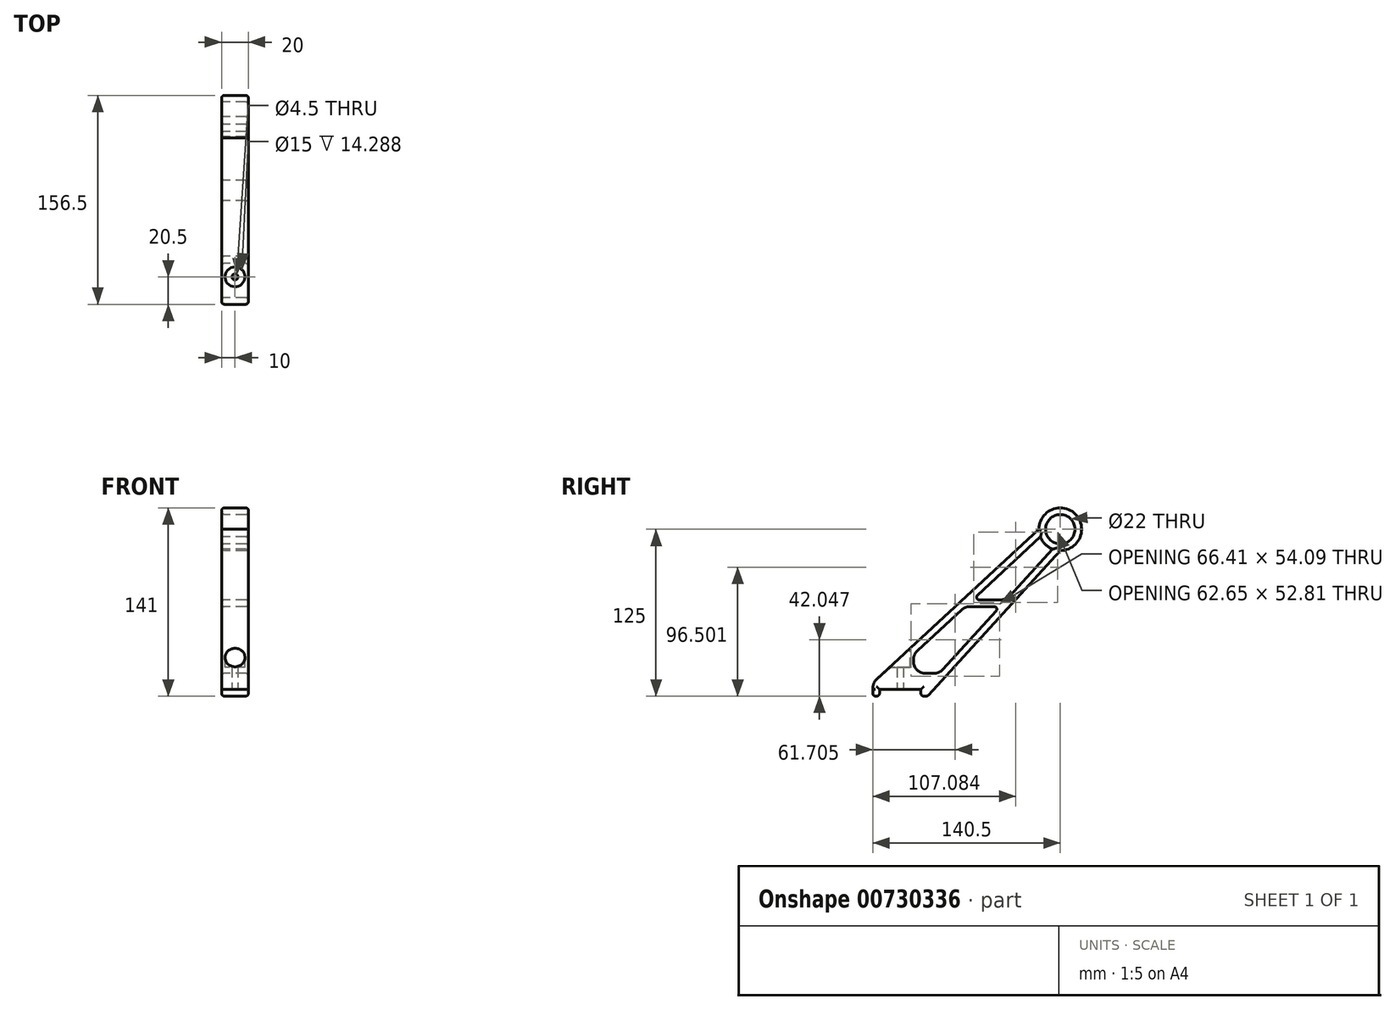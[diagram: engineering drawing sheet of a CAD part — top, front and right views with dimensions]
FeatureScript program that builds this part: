
annotation { "Feature Type Name" : "Feature", "Feature Type Description" : "" }
export const myFeature = defineFeature(function(context is Context, id is Id, definition is map)
    precondition{}
    {
        {
            assignVariable(context, id + "F0", {"name" : "ArmW", "anyValue" : 20});
        }
        {
            var Q0;
            Q0=qCreatedBy(makeId("Right.planeOp"),FACE);
            var sketch = newSketch(context, id + "F1", { "sketchPlane" : qUnion([Q0])});
            skLineSegment(sketch, "E0.bottom", {"start": v(-15.5, 0) * mm, "end": v(15.5, 0) * mm});
            skLineSegment(sketch, "E1.left", {"start": v(-20.47, 1.18) * mm, "end": v(-20.5, 0) * mm});
            skLineSegment(sketch, "E2.left", {"start": v(-20.5, 0) * mm, "end": v(-20.5, -5) * mm});
            skLineSegment(sketch, "E2.right", {"start": v(-15.5, 0) * mm, "end": v(-15.5, -5) * mm});
            skCircle(sketch, "E3", {"center": v(120, 120) * mm, "radius": 11 * mm});
            skCircle(sketch, "E4", {"center": v(120, 120) * mm, "radius": 16 * mm});
            skLineSegment(sketch, "E5.bottom", {"start": v(0, 0) * mm, "end": v(120, 0) * mm, "construction": true});
            skLineSegment(sketch, "E5.top", {"start": v(0, 120) * mm, "end": v(120, 120) * mm, "construction": true});
            skLineSegment(sketch, "E5.left", {"start": v(0, 4.75) * mm, "end": v(0, 120) * mm, "construction": true});
            skLineSegment(sketch, "E5.right", {"start": v(120, 0) * mm, "end": v(120, 120) * mm, "construction": true});
            skLineSegment(sketch, "E6", {"start": v(104, 120) * mm, "end": v(-17.59, 7.6) * mm});
            skLineSegment(sketch, "E7", {"start": v(120, 104) * mm, "end": v(20.5, -5) * mm});
            skLineSegment(sketch, "E8", {"start": v(15.5, 0) * mm, "end": v(15.5, -5) * mm});
            skLineSegment(sketch, "E9", {"start": v(15.5, -5) * mm, "end": v(20.5, -5) * mm});
            skLineSegment(sketch, "E10", {"start": v(-20.5, -5) * mm, "end": v(-15.5, -5) * mm});
            skPoint(sketch, "E11", {"position": v(0, 0) * mm});
            skLineSegment(sketch, "E12", {"start": v(12.9, 28.96) * mm, "end": v(46.14, 59.7) * mm});
            skLineSegment(sketch, "E13", {"start": v(31.93, 14.93) * mm, "end": v(71.92, 58.75) * mm});
            skLineSegment(sketch, "E14", {"start": v(25.28, 12) * mm, "end": v(19, 12) * mm});
            skLineSegment(sketch, "E15", {"start": v(10, 21) * mm, "end": v(10, 22.35) * mm});
            skLineSegment(sketch, "E16", {"start": v(52.25, 62.1) * mm, "end": v(70.44, 62.1) * mm});
            skPoint(sketch, "E17", {"position": v(61.85, 62.1) * mm});
            skLineSegment(sketch, "E18", {"start": v(59.25, 67.1) * mm, "end": v(75.57, 67.1) * mm});
            skPoint(sketch, "E19", {"position": v(66.84, 67.1) * mm});
            skLineSegment(sketch, "E20", {"start": v(10, 26.29) * mm, "end": v(10, 12) * mm});
            skPoint(sketch, "E21.visualSharp", {"position": v(29.25, 12) * mm});
            skArc(sketch, "E21.filletArc", {"start": v(25.28, 12) * mm, "mid": v(28.91, 12.77) * mm, "end": v(31.93, 14.93) * mm});
            skLineSegment(sketch, "E22.trimOffspring", {"start": v(57.9, 70.56) * mm, "end": v(105.09, 114.2) * mm});
            skLineSegment(sketch, "E23.trimOffspring", {"start": v(82.22, 70.03) * mm, "end": v(114.22, 105.08) * mm});
            skPoint(sketch, "E24.visualSharp", {"position": v(48.73, 62.1) * mm});
            skArc(sketch, "E24.filletArc", {"start": v(52.25, 62.1) * mm, "mid": v(48.97, 61.47) * mm, "end": v(46.14, 59.7) * mm});
            skPoint(sketch, "E25.visualSharp", {"position": v(79.54, 67.1) * mm});
            skPoint(sketch, "E26", {"position": v(120, 104) * mm});
            skPoint(sketch, "E27", {"position": v(104, 120) * mm});
            skPoint(sketch, "E28.visualSharp", {"position": v(10, 26.29) * mm});
            skArc(sketch, "E28.filletArc", {"start": v(12.9, 28.96) * mm, "mid": v(10.75, 25.96) * mm, "end": v(10, 22.35) * mm});
            skPoint(sketch, "E29.visualSharp", {"position": v(10, 12) * mm});
            skArc(sketch, "E29.filletArc", {"start": v(10, 21) * mm, "mid": v(12.64, 14.64) * mm, "end": v(19, 12) * mm});
            skPoint(sketch, "E30.visualSharp", {"position": v(74.98, 62.1) * mm});
            skArc(sketch, "E30.filletArc", {"start": v(71.92, 58.75) * mm, "mid": v(72.27, 60.9) * mm, "end": v(70.44, 62.1) * mm});
            skPoint(sketch, "E31.visualSharp", {"position": v(54.14, 67.1) * mm});
            skArc(sketch, "E31.filletArc", {"start": v(57.9, 70.56) * mm, "mid": v(57.39, 68.37) * mm, "end": v(59.25, 67.1) * mm});
            skArc(sketch, "E32.filletArc", {"start": v(75.57, 67.1) * mm, "mid": v(79.2, 67.86) * mm, "end": v(82.22, 70.03) * mm});
            skPoint(sketch, "E33.visualSharp", {"position": v(-20.4, 5) * mm});
            skArc(sketch, "E33.filletArc", {"start": v(-17.59, 7.6) * mm, "mid": v(-19.68, 4.68) * mm, "end": v(-20.47, 1.18) * mm});
            skSolve(sketch);
        }
        {
            var Q0;
            Q0 = qSketchRegion(id + "F1", true);
            extrude(context, id + "F2", {"entities" : qUnion([Q0]), "depth" : (getVariable(context, 'ArmW')) * mm, "offsetDistance" : 25 * mm});
        }
        {
            var Q0;
            Q0=makeQuery(id+"F2.opExtrude","CAP_FACE",FACE,{"disambiguationData":[OSD([sQuery(id+"F1.wireOp",EDGE,"E0.top"),sQuery(id+"F1.wireOp",EDGE,"E0.left"),sQuery(id+"F1.wireOp",EDGE,"E0.right"),sQuery(id+"F1.wireOp",EDGE,"E1.top"),sQuery(id+"F1.wireOp",EDGE,"E1.left"),sQuery(id+"F1.wireOp",EDGE,"NOMvLF7p-otiR-nEAe-fTJC-VMt4UzeXd9s4.top"),sQuery(id+"F1.wireOp",EDGE,"NOMvLF7p-otiR-nEAe-fTJC-VMt4UzeXd9s4.left"),sQuery(id+"F1.wireOp",EDGE,"NOMvLF7p-otiR-nEAe-fTJC-VMt4UzeXd9s4.right"),sQuery(id+"F1.wireOp",EDGE,"E2.top"),sQuery(id+"F1.wireOp",EDGE,"E2.left"),sQuery(id+"F1.wireOp",EDGE,"E2.right"),sQuery(id+"F1.wireOp",EDGE,"ANYR2TeM-pG0v-Sy7E-um98-puJoWqYqz7nG"),sQuery(id+"F1.wireOp",EDGE,"DYsMuk2t-F1yg-EkOE-B9ZC-1FALk9YSir4c"),sQuery(id+"F1.wireOp",EDGE,"ll421e7q-dBxD-7jqP-6ZOg-A462ZdehQbo3"),sQuery(id+"F1.wireOp",EDGE,"fbd24d79-8a35-4fab-bdf5-51f30801ec70.trimOffspring"),sQuery(id+"F1.wireOp",EDGE,"4f573531-568b-457d-87cc-3bfda0ad51ab1.MirrorCS"),sQuery(id+"F1.wireOp",EDGE,"79f8788a-c3f9-4ef8-aa7a-382f7be76f09.trimOffspring"),sQuery(id+"F1.wireOp",EDGE,"E3"),sQuery(id+"F1.wireOp",EDGE,"E4"),sQuery(id+"F1.wireOp",EDGE,"E6"),sQuery(id+"F1.wireOp",EDGE,"E7"),sQuery(id+"F1.wireOp",EDGE,"3807ad3b-ab58-43f6-95fe-ed81e5da2370.filletArc"),sQuery(id+"F1.wireOp",EDGE,"4c582521-ed1f-46d5-8f13-cee76205d209.filletArc")])],"isStart":true});
            var Q1;
            Q1=makeQuery(id+"F2.opExtrude","CAP_FACE",FACE,{"disambiguationData":[OSD([sQuery(id+"F1.wireOp",EDGE,"E0.top"),sQuery(id+"F1.wireOp",EDGE,"E0.left"),sQuery(id+"F1.wireOp",EDGE,"E0.right"),sQuery(id+"F1.wireOp",EDGE,"E1.top"),sQuery(id+"F1.wireOp",EDGE,"E1.left"),sQuery(id+"F1.wireOp",EDGE,"NOMvLF7p-otiR-nEAe-fTJC-VMt4UzeXd9s4.top"),sQuery(id+"F1.wireOp",EDGE,"NOMvLF7p-otiR-nEAe-fTJC-VMt4UzeXd9s4.left"),sQuery(id+"F1.wireOp",EDGE,"NOMvLF7p-otiR-nEAe-fTJC-VMt4UzeXd9s4.right"),sQuery(id+"F1.wireOp",EDGE,"E2.top"),sQuery(id+"F1.wireOp",EDGE,"E2.left"),sQuery(id+"F1.wireOp",EDGE,"E2.right"),sQuery(id+"F1.wireOp",EDGE,"ANYR2TeM-pG0v-Sy7E-um98-puJoWqYqz7nG"),sQuery(id+"F1.wireOp",EDGE,"DYsMuk2t-F1yg-EkOE-B9ZC-1FALk9YSir4c"),sQuery(id+"F1.wireOp",EDGE,"ll421e7q-dBxD-7jqP-6ZOg-A462ZdehQbo3"),sQuery(id+"F1.wireOp",EDGE,"fbd24d79-8a35-4fab-bdf5-51f30801ec70.trimOffspring"),sQuery(id+"F1.wireOp",EDGE,"4f573531-568b-457d-87cc-3bfda0ad51ab1.MirrorCS"),sQuery(id+"F1.wireOp",EDGE,"79f8788a-c3f9-4ef8-aa7a-382f7be76f09.trimOffspring"),sQuery(id+"F1.wireOp",EDGE,"E3"),sQuery(id+"F1.wireOp",EDGE,"E4"),sQuery(id+"F1.wireOp",EDGE,"E6"),sQuery(id+"F1.wireOp",EDGE,"E7"),sQuery(id+"F1.wireOp",EDGE,"3807ad3b-ab58-43f6-95fe-ed81e5da2370.filletArc"),sQuery(id+"F1.wireOp",EDGE,"4c582521-ed1f-46d5-8f13-cee76205d209.filletArc")])],"isStart":false});
            var Q2;
            Q2=makeQuery(id+"F2.opExtrude","SWEPT_FACE",FACE,{"disambiguationData":[OSD([sQuery(id+"F1.wireOp",EDGE,"E10")])]});
            var Q3;
            Q3=makeQuery(id+"F2.opExtrude","SWEPT_FACE",FACE,{"disambiguationData":[OSD([sQuery(id+"F1.wireOp",EDGE,"E9")])]});
            fillet(context, id + "F3", {"entities" : qUnion([Q0, Q1, Q2, Q3]), "radius" : 2 * mm, "tangentPropagation" : true, "allowEdgeOverflow" : false});
        }
        {
            var Q0;
            Q0=makeQuery(id+"F2.opExtrude","SWEPT_FACE",FACE,{"disambiguationData":[OSD([sQuery(id+"F1.wireOp",EDGE,"E0.bottom")])]});
            var sketch = newSketch(context, id + "F4", { "sketchPlane" : qUnion([Q0])});
            skLineSegment(sketch, "E34", {"start": v(18, -15.5) * mm, "end": v(2, 15.5) * mm, "construction": true});
            skLineSegment(sketch, "E35", {"start": v(18, 15.5) * mm, "end": v(2, -15.5) * mm, "construction": true});
            skPoint(sketch, "E36", {"position": v(10, 0) * mm});
            skSolve(sketch);
        }
        {
            var Q0;
            Q0=sQuery(id+"F4.wireOp",VERTEX,"E36");
            var Q1;
            Q1=makeQuery(id+"F2.opExtrude","SWEPT_BODY",BODY,{"disambiguationData":[OSD([sQuery(id+"F1.wireOp",EDGE,"E0.bottom"),sQuery(id+"F1.wireOp",EDGE,"E1.left"),sQuery(id+"F1.wireOp",EDGE,"E2.left"),sQuery(id+"F1.wireOp",EDGE,"E2.right"),sQuery(id+"F1.wireOp",EDGE,"E3"),sQuery(id+"F1.wireOp",EDGE,"E4"),sQuery(id+"F1.wireOp",EDGE,"E6"),sQuery(id+"F1.wireOp",EDGE,"E7"),sQuery(id+"F1.wireOp",EDGE,"4c582521-ed1f-46d5-8f13-cee76205d209.filletArc"),sQuery(id+"F1.wireOp",EDGE,"E8"),sQuery(id+"F1.wireOp",EDGE,"E9"),sQuery(id+"F1.wireOp",EDGE,"E10")])]});
            hole(context, id + "F5", {"style" : HoleStyle.SIMPLE, "endStyle" : HoleEndStyle.THROUGH, "holeDiameter" : 4.5 * mm, "majorDiameter" : 4 * mm, "isTappedThrough" : true, "tappedDepth" : 6.5 * mm, "tapClearance" : 3, "startFromSketch" : true, "locations" : qUnion([Q0]), "scope" : qUnion([Q1])});
        }
        {
            var Q0;
            Q0=qCreatedBy(makeId("Top.planeOp"),FACE);
            cPlane(context, id + "F6", {"entities" : qUnion([Q0]), "cplaneType" : CPlaneType.OFFSET, "offset" : 25 * mm, "width" : 150 * mm, "height" : 150 * mm});
        }
        {
            var Q0;
            Q0=qCreatedBy(id+"F6.planeOp",FACE);
            var sketch = newSketch(context, id + "F7", { "sketchPlane" : qUnion([Q0])});
            skCircle(sketch, "E37.0", {"center": v(10, 0) * mm, "radius": 2.25 * mm});
            skCircle(sketch, "E38", {"center": v(10, 0) * mm, "radius": 7.5 * mm});
            skSolve(sketch);
        }
        {
            var Q0;
            Q0=makeQuery(id+"F7.imprint","IMPRINT",FACE,{"disambiguationData":[TD([[makeQuery(id+"F7.imprint","IMPRINT",EDGE,{"derivedFrom":sQuery(id+"F7.wireOp",EDGE,"E37.0")}),-1.0]])]});
            extrude(context, id + "F8", {"entities" : qUnion([Q0]), "operationType" : NewBodyOperationType.REMOVE, "endBound" : BoundingType.SYMMETRIC, "oppositeDirection" : true, "depth" : 17 * mm, "offsetDistance" : 25 * mm});
        }
    });
